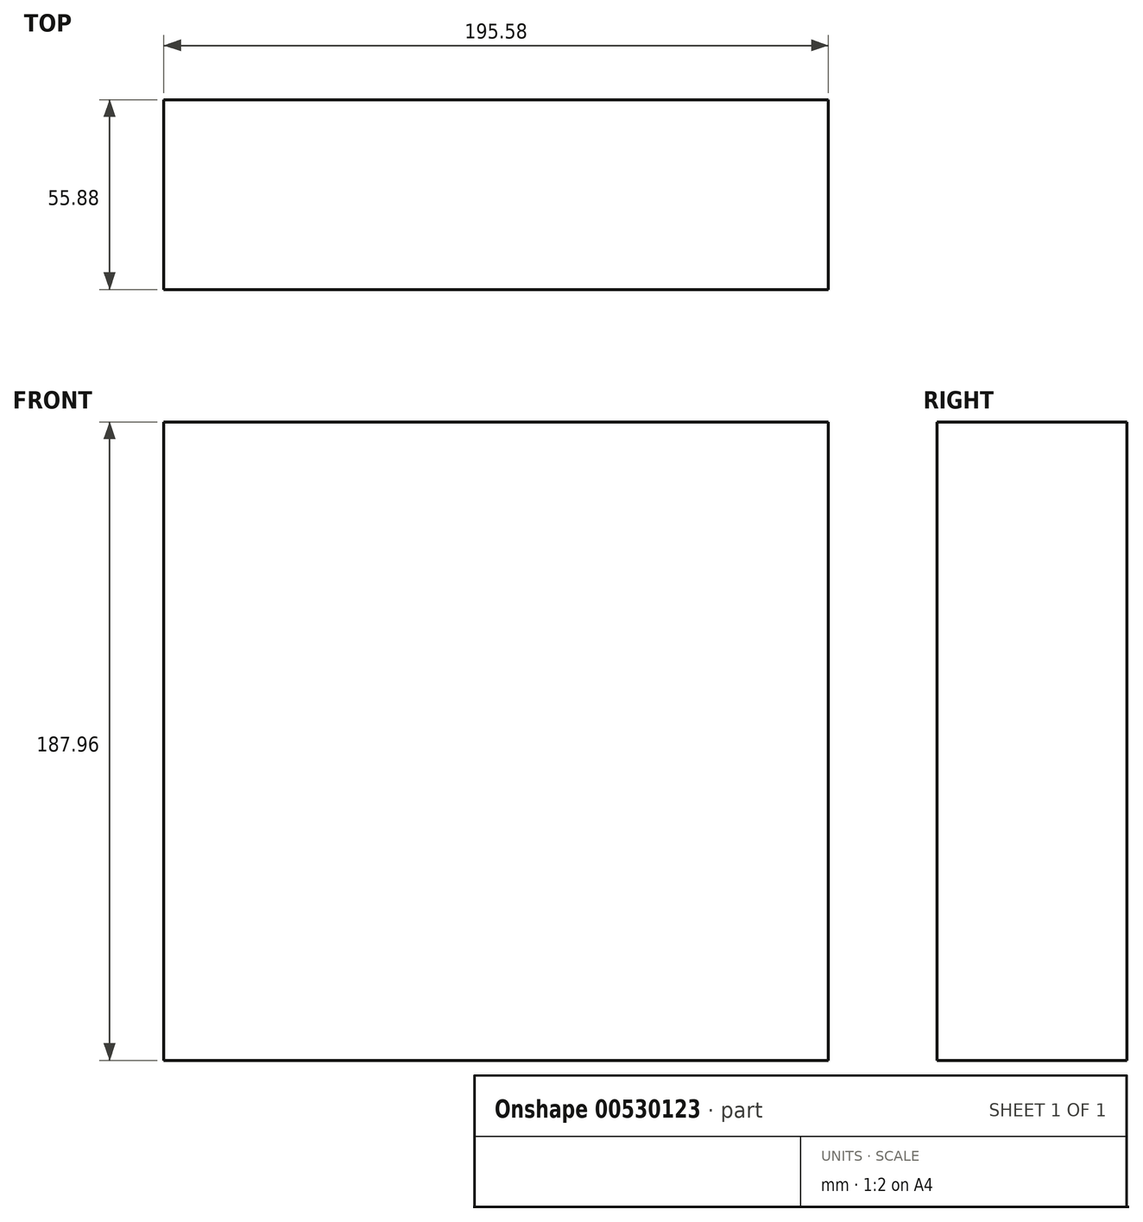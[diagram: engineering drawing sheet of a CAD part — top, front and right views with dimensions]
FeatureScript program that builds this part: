
annotation { "Feature Type Name" : "Feature", "Feature Type Description" : "" }
export const myFeature = defineFeature(function(context is Context, id is Id, definition is map)
    precondition{}
    {
        {
            var Q0;
            Q0=qCreatedBy(makeId("Front.planeOp"),FACE);
            var sketch = newSketch(context, id + "F0", { "sketchPlane" : qUnion([Q0])});
            skLineSegment(sketch, "E0.bottom", {"start": v(-97.8, 93.98) * mm, "end": v(97.8, 93.98) * mm});
            skLineSegment(sketch, "E0.top", {"start": v(-97.8, -93.98) * mm, "end": v(97.79, -93.98) * mm});
            skLineSegment(sketch, "E0.left", {"start": v(-97.8, 93.98) * mm, "end": v(-97.8, -93.98) * mm});
            skLineSegment(sketch, "E0.right", {"start": v(97.8, 93.98) * mm, "end": v(97.79, -93.98) * mm});
            skPoint(sketch, "E0.middle", {"position": v(0, 0) * mm});
            skSolve(sketch);
        }
        {
            var Q0;
            Q0 = qSketchRegion(id + "F0", true);
            extrude(context, id + "F1", {"entities" : qUnion([Q0]), "endBound" : BoundingType.SYMMETRIC, "depth" : 55.88 * mm, "offsetDistance" : 25.4 * mm});
        }
    });
